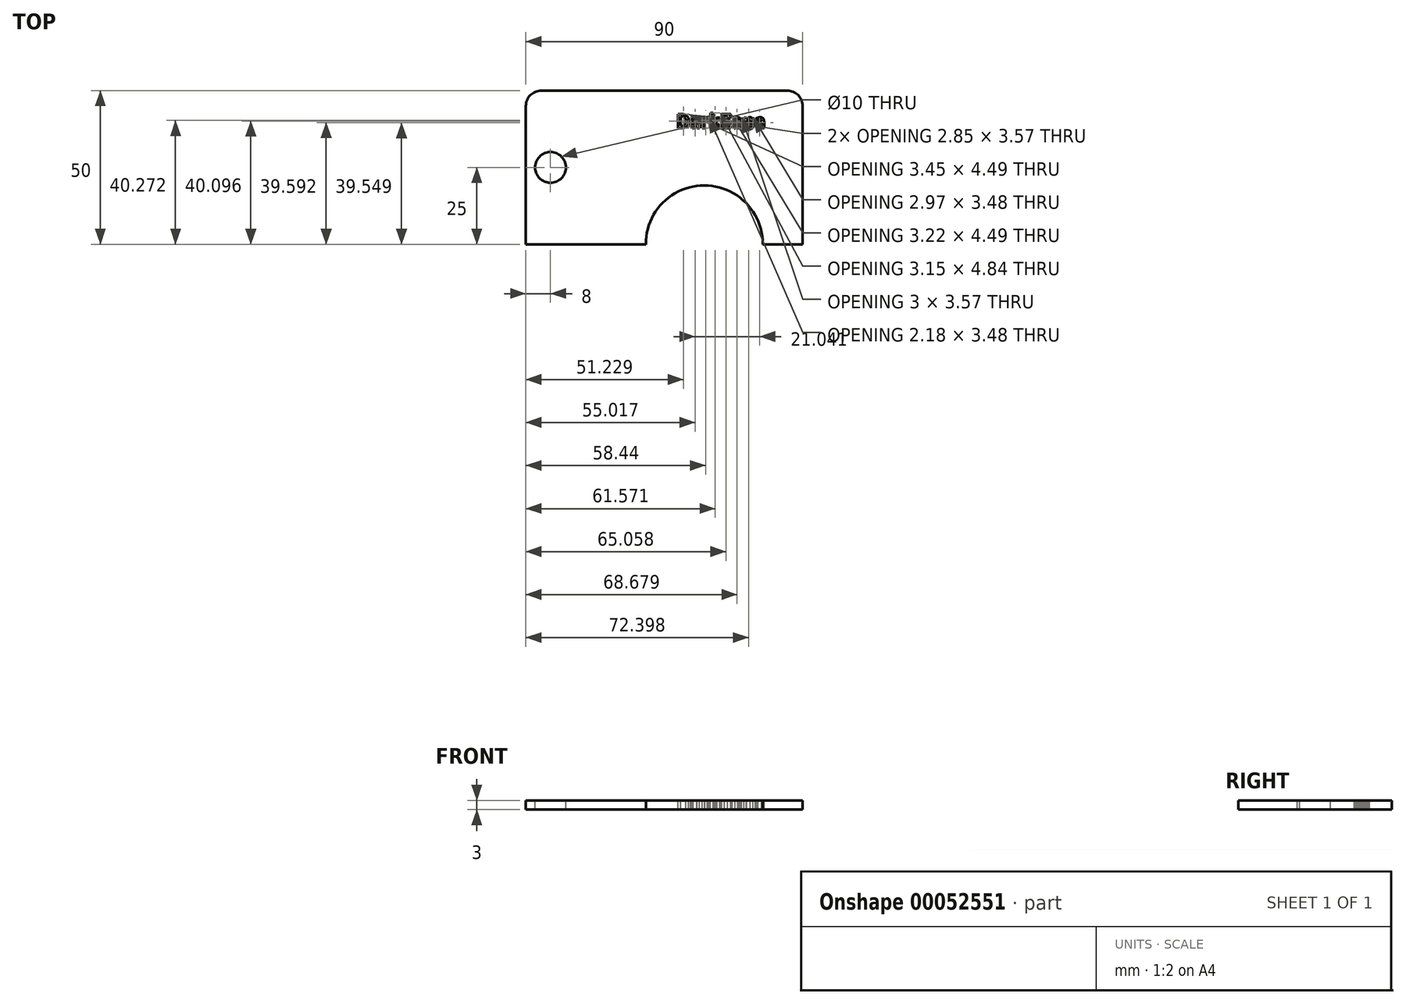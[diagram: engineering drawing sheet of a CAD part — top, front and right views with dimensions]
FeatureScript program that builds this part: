
annotation { "Feature Type Name" : "Feature", "Feature Type Description" : "" }
export const myFeature = defineFeature(function(context is Context, id is Id, definition is map)
    precondition{}
    {
        {
            var Q0;
            Q0=qCreatedBy(makeId("Top.planeOp"),FACE);
            var sketch = newSketch(context, id + "F0", { "sketchPlane" : qUnion([Q0])});
            skLineSegment(sketch, "E0", {"start": v(5, 50) * mm, "end": v(85, 50) * mm});
            skLineSegment(sketch, "E1", {"start": v(90, 45) * mm, "end": v(90, 0) * mm});
            skPoint(sketch, "E2.visualSharp", {"position": v(90, 50) * mm});
            skArc(sketch, "E2.filletArc", {"start": v(90, 45) * mm, "mid": v(88.54, 48.54) * mm, "end": v(85, 50) * mm});
            skPoint(sketch, "E3.center.orphan", {"position": v(39, 0) * mm});
            skPoint(sketch, "E3.end.orphan", {"position": v(0, 0) * mm});
            skPoint(sketch, "E4.start.orphan", {"position": v(20, 0) * mm});
            skLineSegment(sketch, "E5", {"start": v(0, 0) * mm, "end": v(0, 45) * mm});
            skPoint(sketch, "E6.visualSharp", {"position": v(0, 50) * mm});
            skArc(sketch, "E6.filletArc", {"start": v(5, 50) * mm, "mid": v(1.46, 48.54) * mm, "end": v(0, 45) * mm});
            skPoint(sketch, "E7.center.orphan", {"position": v(77, 0) * mm});
            skPoint(sketch, "E8.start.orphan", {"position": v(87, 0) * mm});
            skPoint(sketch, "E9.end.orphan", {"position": v(67, 0) * mm});
            skPoint(sketch, "E9.start.orphan", {"position": v(50, 0) * mm});
            skLineSegment(sketch, "E10", {"start": v(0, 0) * mm, "end": v(39, 0) * mm});
            skLineSegment(sketch, "E11", {"start": v(90, 0) * mm, "end": v(77, 0) * mm});
            skArc(sketch, "E12", {"start": v(77, 0) * mm, "mid": v(58, 19.13) * mm, "end": v(39, 0) * mm});
            skSolve(sketch);
        }
        {
            var Q0;
            Q0=makeQuery(id+"F0.imprint","IMPRINT",FACE,{"disambiguationData":[TD([[makeQuery(id+"F0.imprint","IMPRINT",EDGE,{"derivedFrom":sQuery(id+"F0.wireOp",EDGE,"E0")}),-1.0]])]});
            var Q1;
            Q1=sQuery(id+"F0.wireOp",EDGE,"44cd6f58-2442-4ab2-a66c-49febcd10911");
            var Q2;
            Q2=sQuery(id+"F0.wireOp",EDGE,"E5");
            var Q3;
            Q3=sQuery(id+"F0.wireOp",EDGE,"E0");
            var Q4;
            Q4=sQuery(id+"F0.wireOp",EDGE,"E1");
            var Q5;
            Q5=sQuery(id+"F0.wireOp",EDGE,"E8");
            var Q6;
            Q6=sQuery(id+"F0.wireOp",EDGE,"E7");
            var Q7;
            Q7=sQuery(id+"F0.wireOp",EDGE,"57cde646-e245-466a-bc5e-86c8e6e16d37");
            var Q8;
            Q8=sQuery(id+"F0.wireOp",EDGE,"9c098bcf-ac51-4b07-a6be-ecb029e82614");
            extrude(context, id + "F1", {"entities" : qUnion([Q0]), "surfaceEntities" : qUnion([Q1, Q2, Q3, Q4, Q5, Q6, Q7, Q8]), "depth" : 3 * mm});
        }
        {
            var Q0;
            Q0=makeQuery(id+"F1.opExtrude","CAP_FACE",FACE,{"disambiguationData":[OSD([sQuery(id+"F0.wireOp",EDGE,"E0"),sQuery(id+"F0.wireOp",EDGE,"E1"),sQuery(id+"F0.wireOp",EDGE,"E2.filletArc"),sQuery(id+"F0.wireOp",EDGE,"E7"),sQuery(id+"F0.wireOp",EDGE,"E8"),sQuery(id+"F0.wireOp",EDGE,"9c098bcf-ac51-4b07-a6be-ecb029e82614"),sQuery(id+"F0.wireOp",EDGE,"57cde646-e245-466a-bc5e-86c8e6e16d37"),sQuery(id+"F0.wireOp",EDGE,"44cd6f58-2442-4ab2-a66c-49febcd10911"),sQuery(id+"F0.wireOp",EDGE,"E5")])],"isStart":false});
            var sketch = newSketch(context, id + "F2", { "sketchPlane" : qUnion([Q0])});
            skCircle(sketch, "E13", {"center": v(8, 25) * mm, "radius": 5 * mm});
            skSolve(sketch);
        }
        {
            var Q0;
            Q0=makeQuery(id+"F2.imprint","IMPRINT",FACE,{"disambiguationData":[TD([[makeQuery(id+"F2.imprint","IMPRINT",EDGE,{"derivedFrom":sQuery(id+"F2.wireOp",EDGE,"E13")}),1.0]])]});
            var Q1;
            Q1=sQuery(id+"F2.wireOp",EDGE,"E13");
            extrude(context, id + "F3", {"entities" : qUnion([Q0]), "operationType" : NewBodyOperationType.REMOVE, "surfaceEntities" : qUnion([Q1]), "oppositeDirection" : true, "depth" : 25 * mm});
        }
        {
            var Q0;
            Q0=makeQuery(id+"F1.opExtrude","CAP_FACE",FACE,{"disambiguationData":[OSD([sQuery(id+"F0.wireOp",EDGE,"E0"),sQuery(id+"F0.wireOp",EDGE,"E1"),sQuery(id+"F0.wireOp",EDGE,"E2.filletArc"),sQuery(id+"F0.wireOp",EDGE,"E7"),sQuery(id+"F0.wireOp",EDGE,"E8"),sQuery(id+"F0.wireOp",EDGE,"9c098bcf-ac51-4b07-a6be-ecb029e82614"),sQuery(id+"F0.wireOp",EDGE,"44cd6f58-2442-4ab2-a66c-49febcd10911"),sQuery(id+"F0.wireOp",EDGE,"E5"),sQuery(id+"F0.wireOp",EDGE,"E6.filletArc"),sQuery(id+"F0.wireOp",EDGE,"E9")])],"isStart":false});
            var sketch = newSketch(context, id + "F4", { "sketchPlane" : qUnion([Q0])});
            skText(sketch, "E14", { "text": "DarkZena", "fontName": "NotoSansCJKsc-Bold.otf"});
            const initialGuessF4  = {"E14": [0.04895, 0.03785, 1, 0, 0.00437]};
            skSetInitialGuess(sketch, initialGuessF4);
            skSolve(sketch);
        }
        {
            var Q0;
            Q0 = qSketchRegion(id + "F4", true);
            extrude(context, id + "F5", {"entities" : qUnion([Q0]), "operationType" : NewBodyOperationType.REMOVE, "oppositeDirection" : true, "depth" : 25 * mm});
        }
    });
